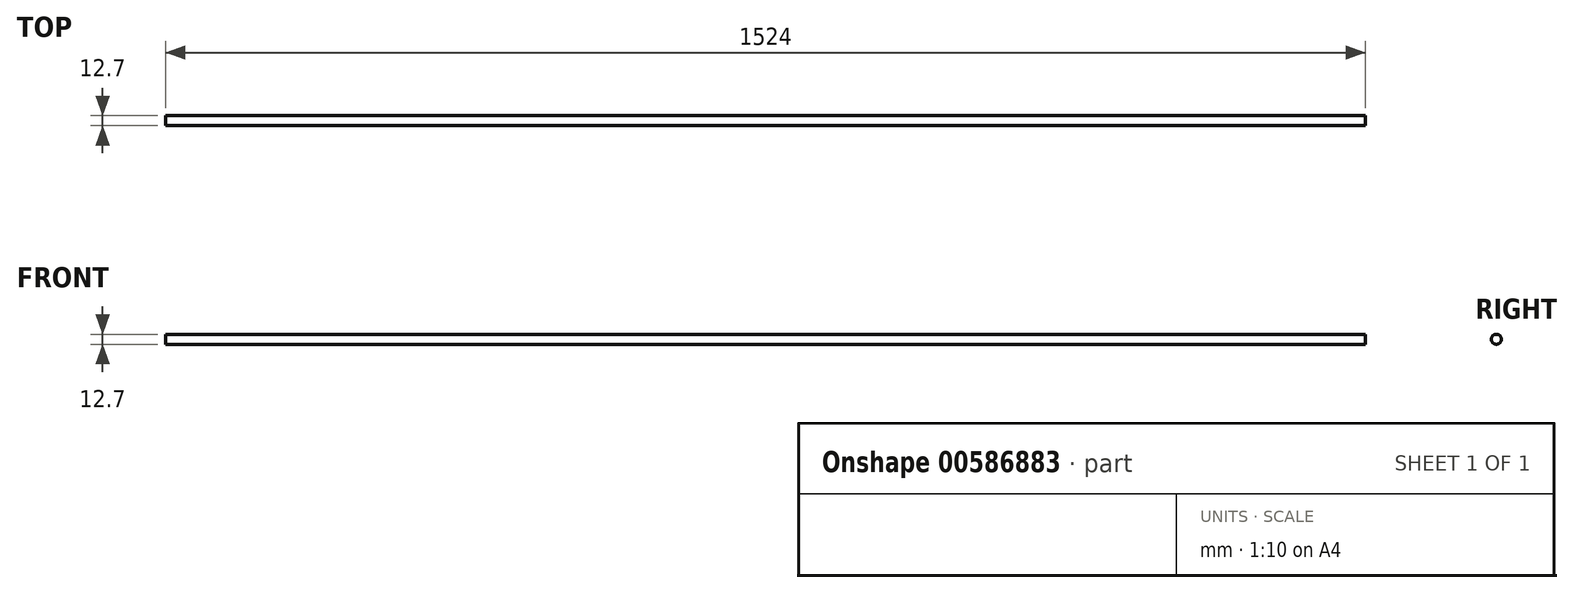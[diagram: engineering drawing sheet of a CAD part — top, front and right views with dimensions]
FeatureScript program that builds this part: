
annotation { "Feature Type Name" : "Feature", "Feature Type Description" : "" }
export const myFeature = defineFeature(function(context is Context, id is Id, definition is map)
    precondition{}
    {
        {
            var Q0;
            Q0=qCreatedBy(makeId("Right.planeOp"),FACE);
            var sketch = newSketch(context, id + "F0", { "sketchPlane" : qUnion([Q0])});
            skCircle(sketch, "E0", {"center": v(0, 0) * mm, "radius": 6.35 * mm});
            skSolve(sketch);
        }
        {
            var Q0;
            Q0 = qSketchRegion(id + "F0", true);
            extrude(context, id + "F1", {"entities" : qUnion([Q0]), "endBound" : BoundingType.SYMMETRIC, "depth" : 1524 * mm, "offsetDistance" : 25.4 * mm});
        }
    });
